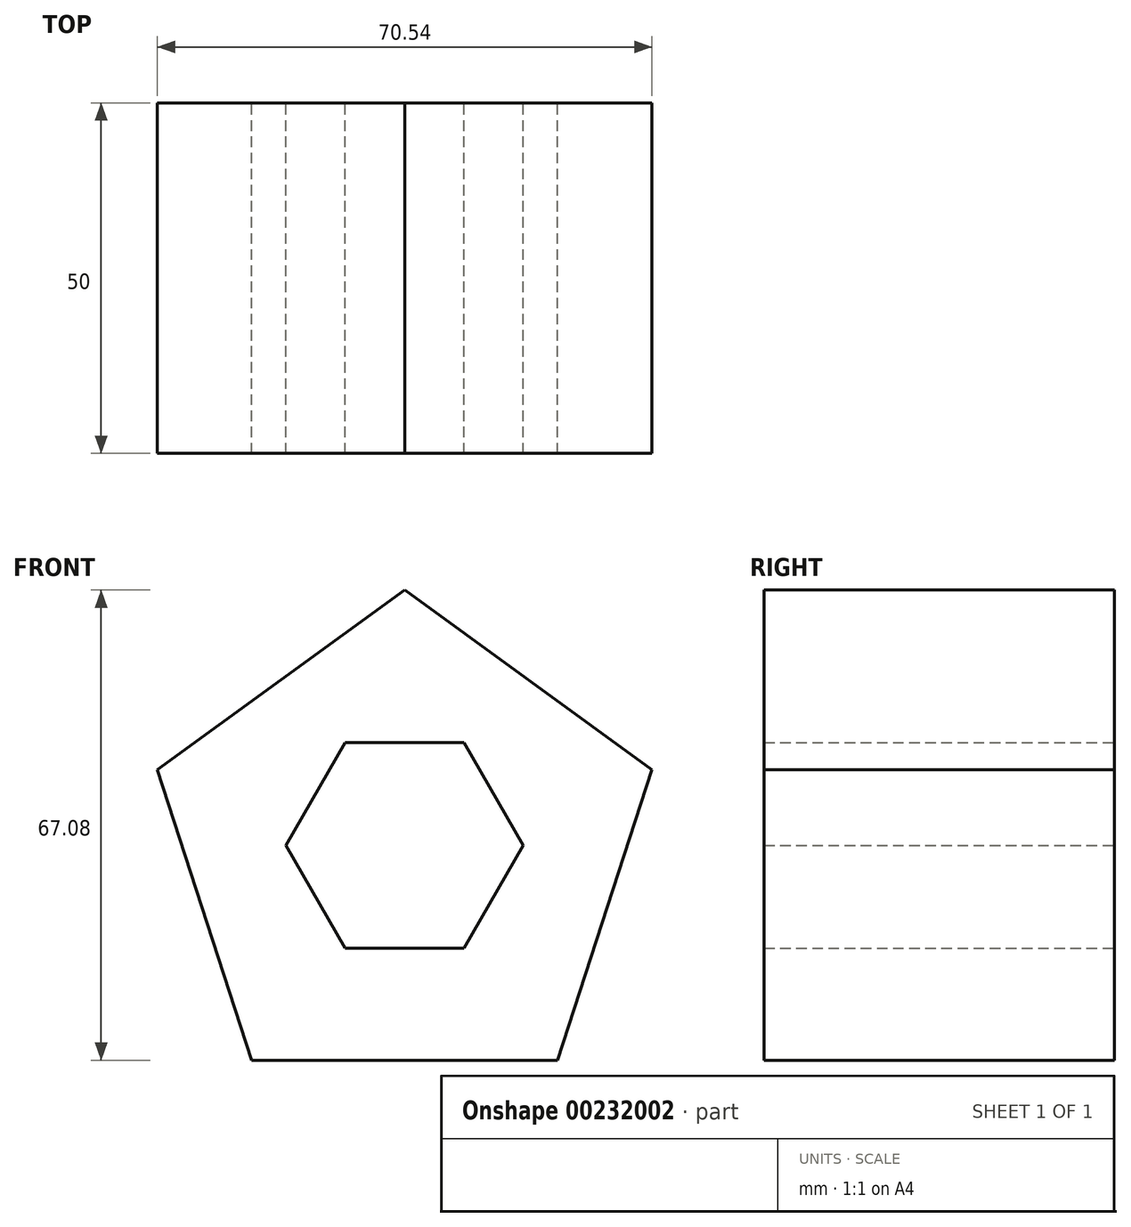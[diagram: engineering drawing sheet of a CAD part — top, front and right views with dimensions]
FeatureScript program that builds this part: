
annotation { "Feature Type Name" : "Feature", "Feature Type Description" : "" }
export const myFeature = defineFeature(function(context is Context, id is Id, definition is map)
    precondition{}
    {
        {
            var Q0;
            Q0=qCreatedBy(makeId("Front.planeOp"),FACE);
            var sketch = newSketch(context, id + "F0", { "sketchPlane" : qUnion([Q0])});
            skLineSegment(sketch, "E0", {"start": v(-21.8, -30) * mm, "end": v(21.8, -30) * mm});
            skLineSegment(sketch, "E1", {"start": v(-21.8, -30) * mm, "end": v(-35.27, 11.46) * mm});
            skLineSegment(sketch, "E2", {"start": v(-35.27, 11.46) * mm, "end": v(0, 37.08) * mm});
            skLineSegment(sketch, "E3", {"start": v(0, 37.08) * mm, "end": v(35.27, 11.46) * mm});
            skLineSegment(sketch, "E4", {"start": v(21.8, -30) * mm, "end": v(35.27, 11.46) * mm});
            skLineSegment(sketch, "E5", {"start": v(-8.47, 15.33) * mm, "end": v(8.47, 15.33) * mm});
            skLineSegment(sketch, "E6", {"start": v(-8.47, 15.33) * mm, "end": v(-16.93, 0.67) * mm});
            skLineSegment(sketch, "E7", {"start": v(-16.93, 0.67) * mm, "end": v(-8.47, -14) * mm});
            skLineSegment(sketch, "E8", {"start": v(-8.47, -14) * mm, "end": v(8.47, -14) * mm});
            skLineSegment(sketch, "E9", {"start": v(8.47, 15.33) * mm, "end": v(16.93, 0.67) * mm});
            skLineSegment(sketch, "E10", {"start": v(8.47, -14) * mm, "end": v(16.93, 0.67) * mm});
            skPoint(sketch, "E11.center.orphan", {"position": v(0, 0) * mm});
            skCircle(sketch, "E12", {"center": v(0, 0) * mm, "radius": 30 * mm, "construction": true});
            skCircle(sketch, "E13", {"center": v(0, 0) * mm, "radius": 15 * mm, "construction": true});
            skSolve(sketch);
        }
        {
            var Q0;
            Q0 = qSketchRegion(id + "F0", true);
            extrude(context, id + "F1", {"entities" : qUnion([Q0]), "depth" : 50 * mm});
        }
    });
